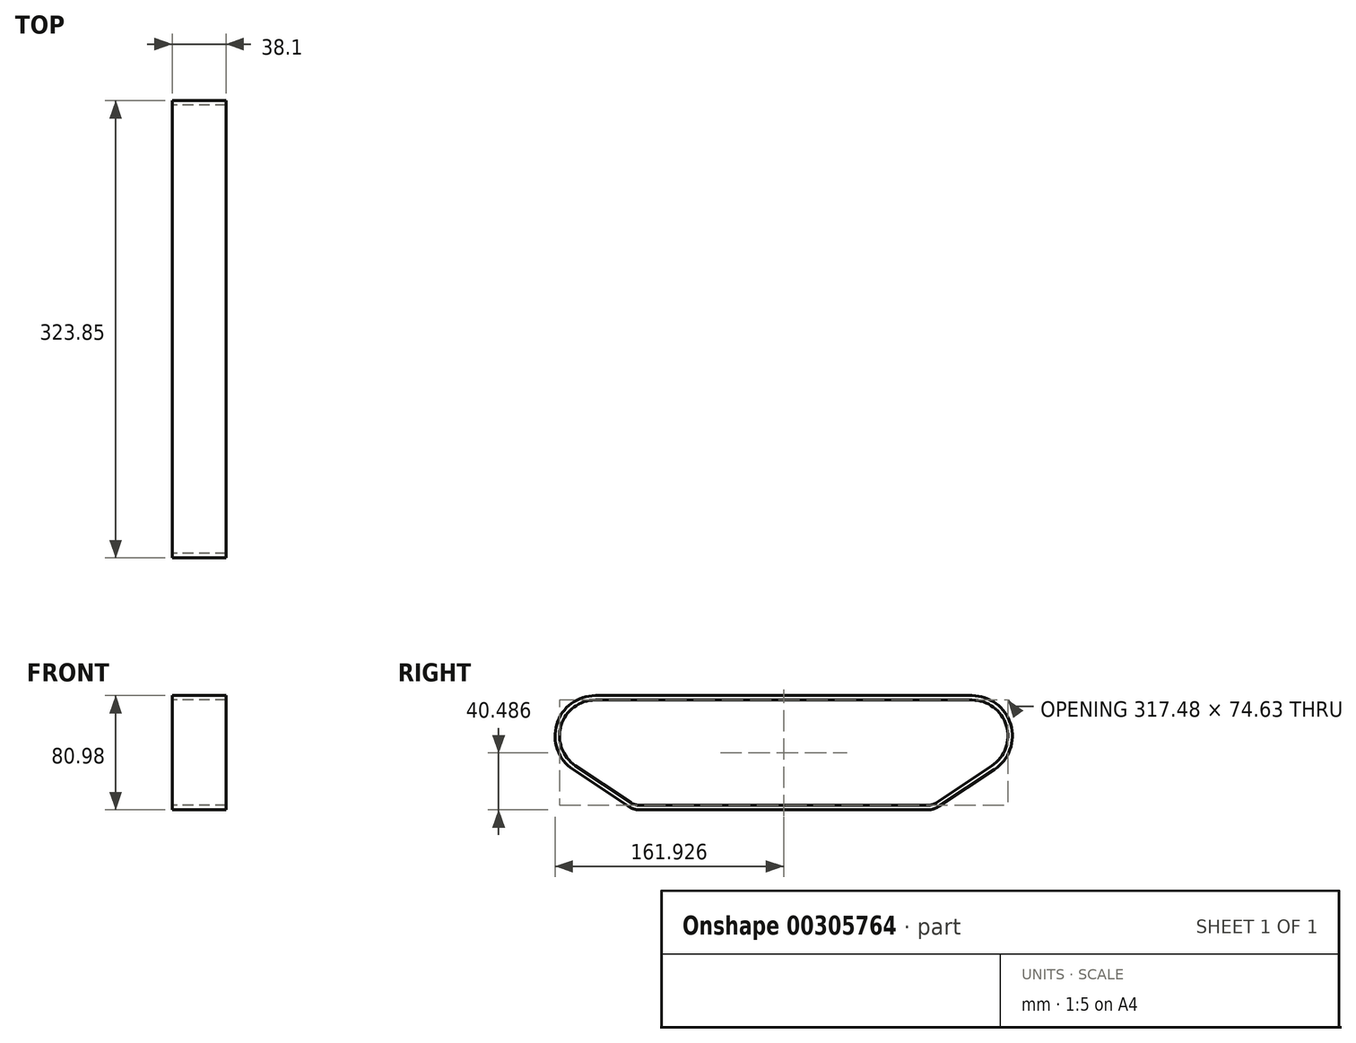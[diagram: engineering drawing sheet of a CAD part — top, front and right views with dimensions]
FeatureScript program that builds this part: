
annotation { "Feature Type Name" : "Feature", "Feature Type Description" : "" }
export const myFeature = defineFeature(function(context is Context, id is Id, definition is map)
    precondition{}
    {
        {
            var Q0;
            Q0=qCreatedBy(makeId("Right.planeOp"),FACE);
            var sketch = newSketch(context, id + "F0", { "sketchPlane" : qUnion([Q0])});
            skArc(sketch, "E0", {"start": v(-179.42, -11.63) * mm, "mid": v(-203.73, -29.67) * mm, "end": v(-193.51, -58.16) * mm});
            skLineSegment(sketch, "E1", {"start": v(-179.42, -11.63) * mm, "end": v(87.28, -11.63) * mm});
            skArc(sketch, "E2", {"start": v(101.36, -58.16) * mm, "mid": v(111.59, -29.67) * mm, "end": v(87.28, -11.63) * mm});
            skArc(sketch, "E3", {"start": v(-154.38, -84.25) * mm, "mid": v(-151.2, -85.75) * mm, "end": v(-147.72, -86.26) * mm});
            skArc(sketch, "E4", {"start": v(55.58, -86.26) * mm, "mid": v(59.05, -85.75) * mm, "end": v(62.23, -84.25) * mm});
            skLineSegment(sketch, "E5", {"start": v(-193.51, -58.16) * mm, "end": v(-154.38, -84.25) * mm});
            skLineSegment(sketch, "E6", {"start": v(101.36, -58.16) * mm, "end": v(62.23, -84.25) * mm});
            skLineSegment(sketch, "E7", {"start": v(-147.72, -86.26) * mm, "end": v(55.58, -86.26) * mm});
            skArc(sketch, "E8.0", {"start": v(-179.42, -8.45) * mm, "mid": v(-206.77, -28.75) * mm, "end": v(-195.27, -60.8) * mm});
            skLineSegment(sketch, "E8.1", {"start": v(-195.27, -60.8) * mm, "end": v(-156.14, -86.89) * mm});
            skLineSegment(sketch, "E8.2", {"start": v(-179.42, -8.45) * mm, "end": v(87.28, -8.45) * mm});
            skArc(sketch, "E8.3", {"start": v(-156.14, -86.89) * mm, "mid": v(-152.12, -88.78) * mm, "end": v(-147.72, -89.43) * mm});
            skArc(sketch, "E8.4", {"start": v(103.12, -60.8) * mm, "mid": v(114.63, -28.75) * mm, "end": v(87.28, -8.45) * mm});
            skLineSegment(sketch, "E8.5", {"start": v(103.12, -60.8) * mm, "end": v(64, -86.89) * mm});
            skArc(sketch, "E8.6", {"start": v(55.58, -89.43) * mm, "mid": v(59.97, -88.78) * mm, "end": v(64, -86.89) * mm});
            skLineSegment(sketch, "E8.7", {"start": v(-147.72, -89.43) * mm, "end": v(55.58, -89.43) * mm});
            skSolve(sketch);
        }
        {
            var Q0;
            Q0=qSketchRegion(id+"F0",true);
            extrude(context, id + "F1", {"entities" : qUnion([Q0]), "depth" : 38.1 * mm});
        }
    });
